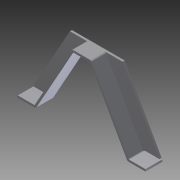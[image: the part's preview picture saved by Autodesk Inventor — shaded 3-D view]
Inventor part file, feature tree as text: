
AUTODESK INVENTOR PART (.ipt)
format: ipt  version: 2012 (Build 160160000, 160)  size: 121,344 bytes
history: native  units: in
note: dims shown in document units (in); Inventor stores cm internally (conversion verified against a paired STEP export)
features: extrude x2, fillet x2, sketch x1
ambient origin geometry x8: Origin, YZ Plane, XZ Plane, XY Plane, X Axis, Y Axis, Z Axis, Center Point
bodies: Solid1 (feature_tree)
feature tree (5):
  sketch  "Sketch1"  dims[d0=7.625in d1=1.0in d2=1.0in d3=1.0in d4=0.125in d5=0.125in d6=4.0in d7=0.0625in d8=0.0625in d9=0.0625in d10=1.0in d11=0.0in d12=0.125in d13=0.0in d14=0.0625in d15=0.125in]
  extrude  "Extrusion1"  Depth=1.0in
  extrude  "Extrusion2"  Depth=1.0in
  fillet  "Fillet1"  Radius=1.0in
  fillet  "Fillet2"  Radius=0.125in
